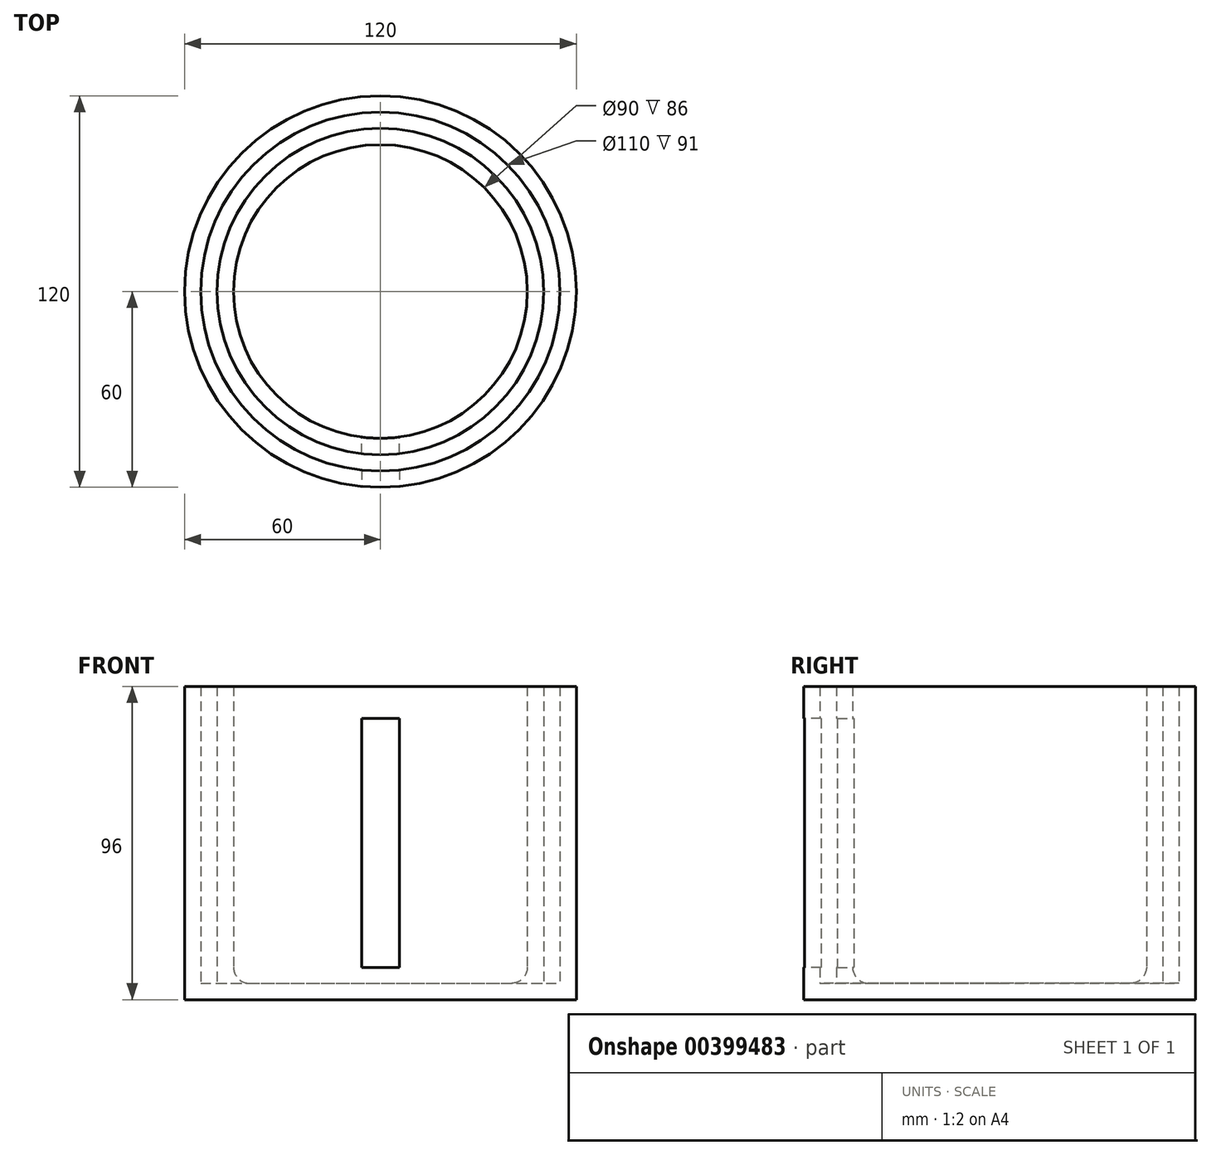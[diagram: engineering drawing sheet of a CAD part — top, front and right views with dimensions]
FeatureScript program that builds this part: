
annotation { "Feature Type Name" : "Feature", "Feature Type Description" : "" }
export const myFeature = defineFeature(function(context is Context, id is Id, definition is map)
    precondition{}
    {
        {
            var Q0;
            Q0=qCreatedBy(makeId("Front.planeOp"),FACE);
            var sketch = newSketch(context, id + "F0", { "sketchPlane" : qUnion([Q0])});
            skLineSegment(sketch, "E0", {"start": v(0, 0) * mm, "end": v(60, 0) * mm});
            skLineSegment(sketch, "E1", {"start": v(60, 0) * mm, "end": v(60, 96) * mm});
            skLineSegment(sketch, "E2.0", {"start": v(55, 5) * mm, "end": v(55, 96) * mm});
            skLineSegment(sketch, "E2.1", {"start": v(0, 5) * mm, "end": v(40, 5) * mm});
            skLineSegment(sketch, "E3", {"start": v(60, 96) * mm, "end": v(55, 96) * mm});
            skLineSegment(sketch, "E4", {"start": v(0, 0) * mm, "end": v(0, 5) * mm});
            skLineSegment(sketch, "E5.top", {"start": v(45, 96) * mm, "end": v(50, 96) * mm});
            skLineSegment(sketch, "E5.left", {"start": v(45, 10) * mm, "end": v(45, 96) * mm});
            skLineSegment(sketch, "E5.right", {"start": v(50, 5) * mm, "end": v(50, 96) * mm});
            skLineSegment(sketch, "E6.trimOffspring", {"start": v(50, 5) * mm, "end": v(55, 5) * mm});
            skPoint(sketch, "E7.visualSharp", {"position": v(45, 5) * mm});
            skArc(sketch, "E7.filletArc", {"start": v(40, 5) * mm, "mid": v(43.54, 6.46) * mm, "end": v(45, 10) * mm});
            skSolve(sketch);
        }
        {
            var Q0;
            Q0=makeQuery(id+"F0.imprint","IMPRINT",FACE,{"disambiguationData":[TD([[makeQuery(id+"F0.imprint","IMPRINT",EDGE,{"derivedFrom":sQuery(id+"F0.wireOp",EDGE,"E0")}),1.0]])]});
            var Q1;
            Q1=sQuery(id+"F0.wireOp",EDGE,"E4");
            revolve(context, id + "F1", {"entities" : qUnion([Q0]), "axis" : qUnion([Q1]), "revolveType" : RevolveType.FULL});
        }
        {
            var Q0;
            Q0=qCreatedBy(makeId("Front.planeOp"),FACE);
            var sketch = newSketch(context, id + "F2", { "sketchPlane" : qUnion([Q0])});
            skLineSegment(sketch, "E8.0", {"start": v(55, 5) * mm, "end": v(-55, 5) * mm, "construction": true});
            skLineSegment(sketch, "E9", {"start": v(-60, 0) * mm, "end": v(-60, 96) * mm, "construction": true});
            skLineSegment(sketch, "E10.bottom", {"start": v(5.79, 86.17) * mm, "end": v(-5.79, 86.17) * mm});
            skLineSegment(sketch, "E10.top", {"start": v(5.79, 9.83) * mm, "end": v(-5.79, 9.83) * mm});
            skLineSegment(sketch, "E10.left", {"start": v(5.79, 86.17) * mm, "end": v(5.79, 9.83) * mm});
            skLineSegment(sketch, "E10.right", {"start": v(-5.79, 86.17) * mm, "end": v(-5.79, 9.83) * mm});
            skPoint(sketch, "E10.middle", {"position": v(0, 48) * mm});
            skPoint(sketch, "E10.middle.positionSnap0", {"position": v(-60, 48) * mm});
            skPoint(sketch, "E10.centerSnap0", {"position": v(-60, 48) * mm});
            skSolve(sketch);
        }
        {
            var Q0;
            Q0 = qSketchRegion(id + "F2", true);
            var Q1;
            Q1=makeQuery(id+"F1.opRevolve","SWEPT_FACE",FACE,{"disambiguationData":[OSD([sQuery(id+"F0.wireOp",EDGE,"E5.right")])]});
            extrude(context, id + "F3", {"entities" : qUnion([Q0]), "operationType" : NewBodyOperationType.REMOVE, "endBound" : BoundingType.UP_TO_SURFACE, "endBoundEntityFace" : qUnion([Q1]), "depth" : 25 * mm});
        }
        {
            var Q0;
            Q0=qCreatedBy(makeId("Front.planeOp"),FACE);
            cPlane(context, id + "F4", {"entities" : qUnion([Q0]), "cplaneType" : CPlaneType.OFFSET, "offset" : 75 * mm, "width" : 150 * mm, "height" : 150 * mm});
        }
        {
            var Q0;
            Q0=qCreatedBy(id+"F4.planeOp",FACE);
            var sketch = newSketch(context, id + "F5", { "sketchPlane" : qUnion([Q0])});
            skLineSegment(sketch, "E11.0", {"start": v(-5.79, 86.17) * mm, "end": v(-5.79, 9.83) * mm});
            skPoint(sketch, "E12.0", {"position": v(0, 86.17) * mm});
            skLineSegment(sketch, "E13.0", {"start": v(5.79, 86.17) * mm, "end": v(-5.79, 86.17) * mm});
            skLineSegment(sketch, "E14.0", {"start": v(5.79, 86.17) * mm, "end": v(5.79, 9.83) * mm});
            skLineSegment(sketch, "E15.0", {"start": v(5.79, 9.83) * mm, "end": v(-5.79, 9.83) * mm});
            skSolve(sketch);
        }
        {
            var Q0;
            Q0 = qSketchRegion(id + "F5", true);
            var Q1;
            Q1=makeQuery(id+"F1.opRevolve","SWEPT_FACE",FACE,{"disambiguationData":[OSD([sQuery(id+"F0.wireOp",EDGE,"E2.0")])]});
            extrude(context, id + "F6", {"entities" : qUnion([Q0]), "operationType" : NewBodyOperationType.REMOVE, "endBound" : BoundingType.UP_TO_SURFACE, "oppositeDirection" : true, "endBoundEntityFace" : qUnion([Q1]), "depth" : 25 * mm});
        }
    });
